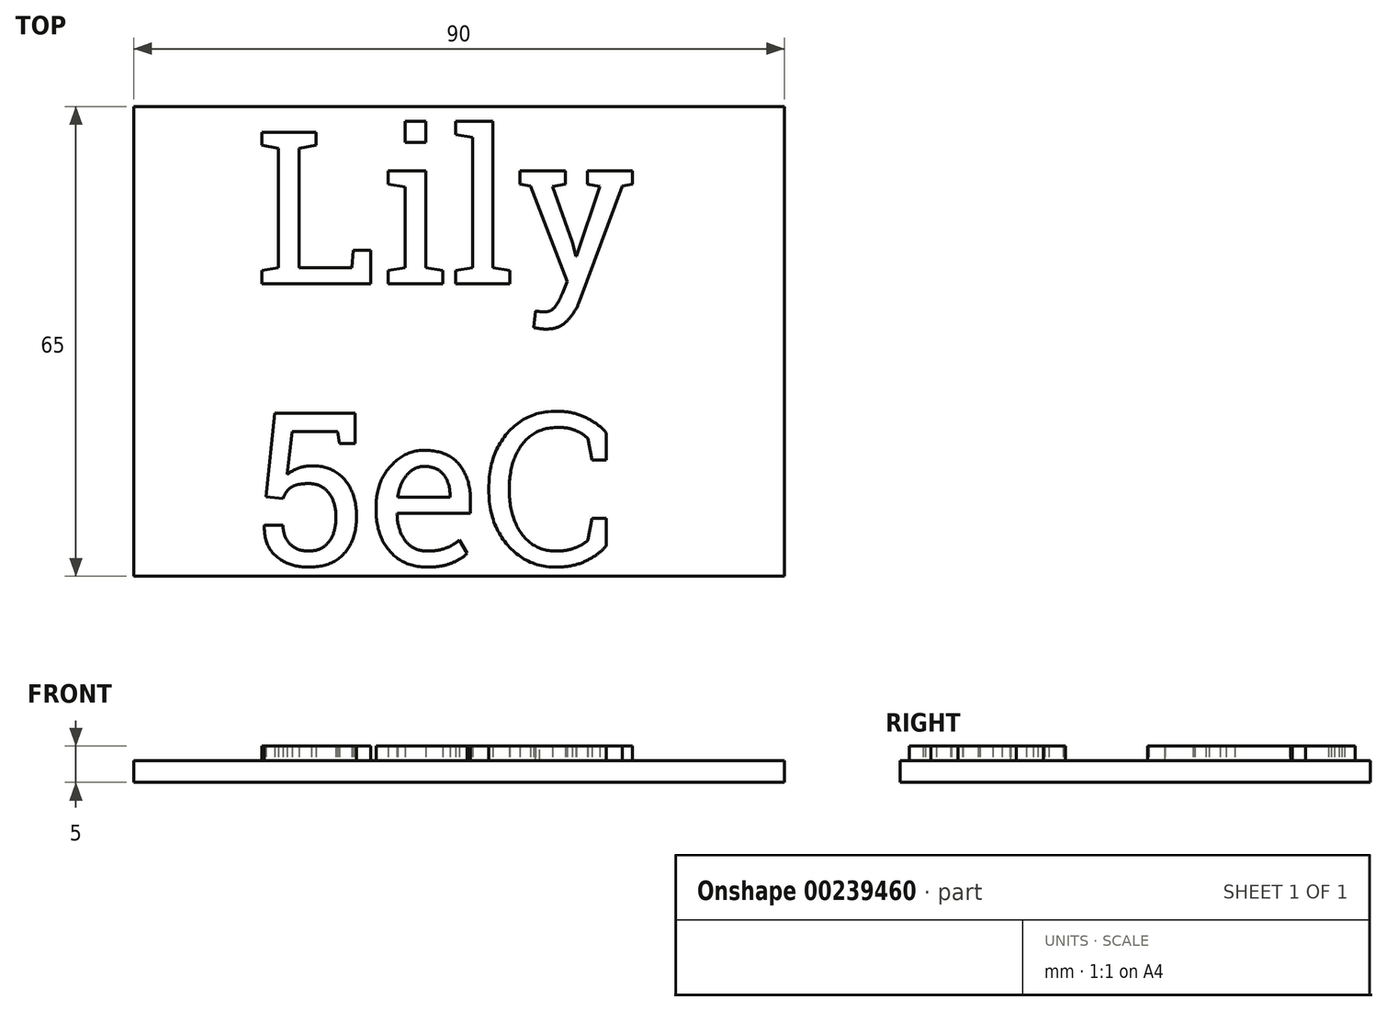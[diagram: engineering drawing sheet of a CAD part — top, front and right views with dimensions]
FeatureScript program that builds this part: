
annotation { "Feature Type Name" : "Feature", "Feature Type Description" : "" }
export const myFeature = defineFeature(function(context is Context, id is Id, definition is map)
    precondition{}
    {
        {
            var Q0;
            Q0=qCreatedBy(makeId("Top.planeOp"),FACE);
            var sketch = newSketch(context, id + "F0", { "sketchPlane" : qUnion([Q0])});
            skLineSegment(sketch, "E0.bottom", {"start": v(0, 0) * mm, "end": v(90, 0) * mm});
            skLineSegment(sketch, "E0.top", {"start": v(0, -65) * mm, "end": v(90, -65) * mm});
            skLineSegment(sketch, "E0.left", {"start": v(0, 0) * mm, "end": v(0, -65) * mm});
            skLineSegment(sketch, "E0.right", {"start": v(90, 0) * mm, "end": v(90, -65) * mm});
            skSolve(sketch);
        }
        {
            var Q0;
            Q0=makeQuery(id+"F0.imprint","IMPRINT",FACE,{"disambiguationData":[TD([[makeQuery(id+"F0.imprint","IMPRINT",EDGE,{"derivedFrom":sQuery(id+"F0.wireOp",EDGE,"E0.bottom")}),-1.0]])]});
            extrude(context, id + "F1", {"entities" : qUnion([Q0]), "depth" : 3 * mm});
        }
        {
            var Q0;
            Q0=makeQuery(id+"F1.opExtrude","CAP_FACE",FACE,{"disambiguationData":[OSD([sQuery(id+"F0.wireOp",EDGE,"E0.bottom"),sQuery(id+"F0.wireOp",EDGE,"E0.top"),sQuery(id+"F0.wireOp",EDGE,"E0.left"),sQuery(id+"F0.wireOp",EDGE,"E0.right")])],"isStart":false});
            var sketch = newSketch(context, id + "F2", { "sketchPlane" : qUnion([Q0])});
            skText(sketch, "E1", { "text": "Lily\n5eC", "fontName": "RobotoSlab-Regular.ttf"});
            const initialGuessF2  = {"E1": [0.01668, -0.02451, 1, 0, 0.02123]};
            skSetInitialGuess(sketch, initialGuessF2);
            skSolve(sketch);
        }
        {
            var Q0;
            Q0 = qSketchRegion(id + "F2", true);
            extrude(context, id + "F3", {"entities" : qUnion([Q0]), "operationType" : NewBodyOperationType.ADD, "depth" : 2 * mm});
        }
    });
